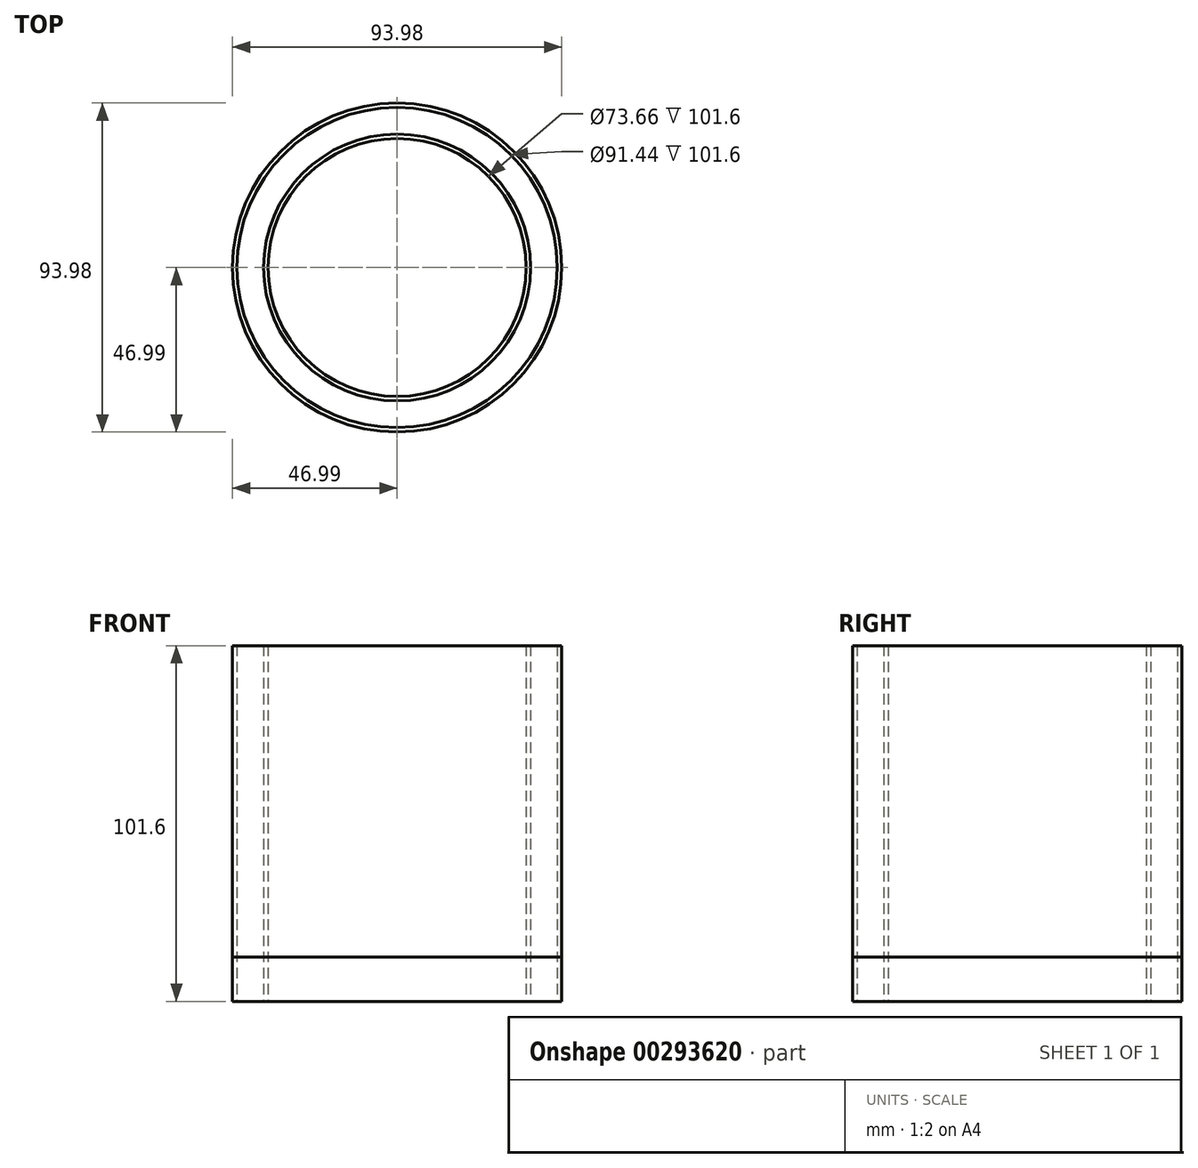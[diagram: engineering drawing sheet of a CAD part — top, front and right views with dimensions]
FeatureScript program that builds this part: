
annotation { "Feature Type Name" : "Feature", "Feature Type Description" : "" }
export const myFeature = defineFeature(function(context is Context, id is Id, definition is map)
    precondition{}
    {
        {
            var Q0;
            Q0=qCreatedBy(makeId("Top.planeOp"),FACE);
            var sketch = newSketch(context, id + "F0", { "sketchPlane" : qUnion([Q0])});
            skCircle(sketch, "E0", {"center": v(0, 0) * mm, "radius": 47 * mm});
            skCircle(sketch, "E1", {"center": v(0, 0) * mm, "radius": 45.72 * mm});
            skCircle(sketch, "E2", {"center": v(0, 0) * mm, "radius": 38.1 * mm});
            skCircle(sketch, "E3", {"center": v(0, 0) * mm, "radius": 36.83 * mm});
            skSolve(sketch);
        }
        {
            var Q0;
            Q0=makeQuery(id+"F0.imprint","IMPRINT",FACE,{"disambiguationData":[TD([[makeQuery(id+"F0.imprint","IMPRINT",EDGE,{"derivedFrom":sQuery(id+"F0.wireOp",EDGE,"E0")}),1.0]])]});
            extrude(context, id + "F1", {"entities" : qUnion([Q0]), "depth" : 101.6 * mm});
        }
        {
            var Q0;
            Q0=qCreatedBy(makeId("Top.planeOp"),FACE);
            var sketch = newSketch(context, id + "F2", { "sketchPlane" : qUnion([Q0])});
            skCircle(sketch, "E4", {"center": v(0, 0) * mm, "radius": 38.1 * mm});
            skCircle(sketch, "E5", {"center": v(0, 0) * mm, "radius": 36.83 * mm});
            skSolve(sketch);
        }
        {
            var Q0;
            Q0=makeQuery(id+"F2.imprint","IMPRINT",FACE,{"disambiguationData":[TD([[makeQuery(id+"F2.imprint","IMPRINT",EDGE,{"derivedFrom":sQuery(id+"F2.wireOp",EDGE,"E4")}),1.0]])]});
            extrude(context, id + "F3", {"entities" : qUnion([Q0]), "depth" : 101.6 * mm});
        }
        {
            var Q0;
            Q0=qCreatedBy(makeId("Top.planeOp"),FACE);
            var sketch = newSketch(context, id + "F4", { "sketchPlane" : qUnion([Q0])});
            skCircle(sketch, "E6", {"center": v(0, 0) * mm, "radius": 47 * mm});
            skSolve(sketch);
        }
        {
            var Q0;
            Q0=makeQuery(id+"F4.imprint","IMPRINT",FACE,{"disambiguationData":[TD([[makeQuery(id+"F4.imprint","IMPRINT",EDGE,{"derivedFrom":sQuery(id+"F4.wireOp",EDGE,"E6")}),1.0]])]});
            extrude(context, id + "F5", {"entities" : qUnion([Q0]), "depth" : 12.7 * mm});
        }
    });
